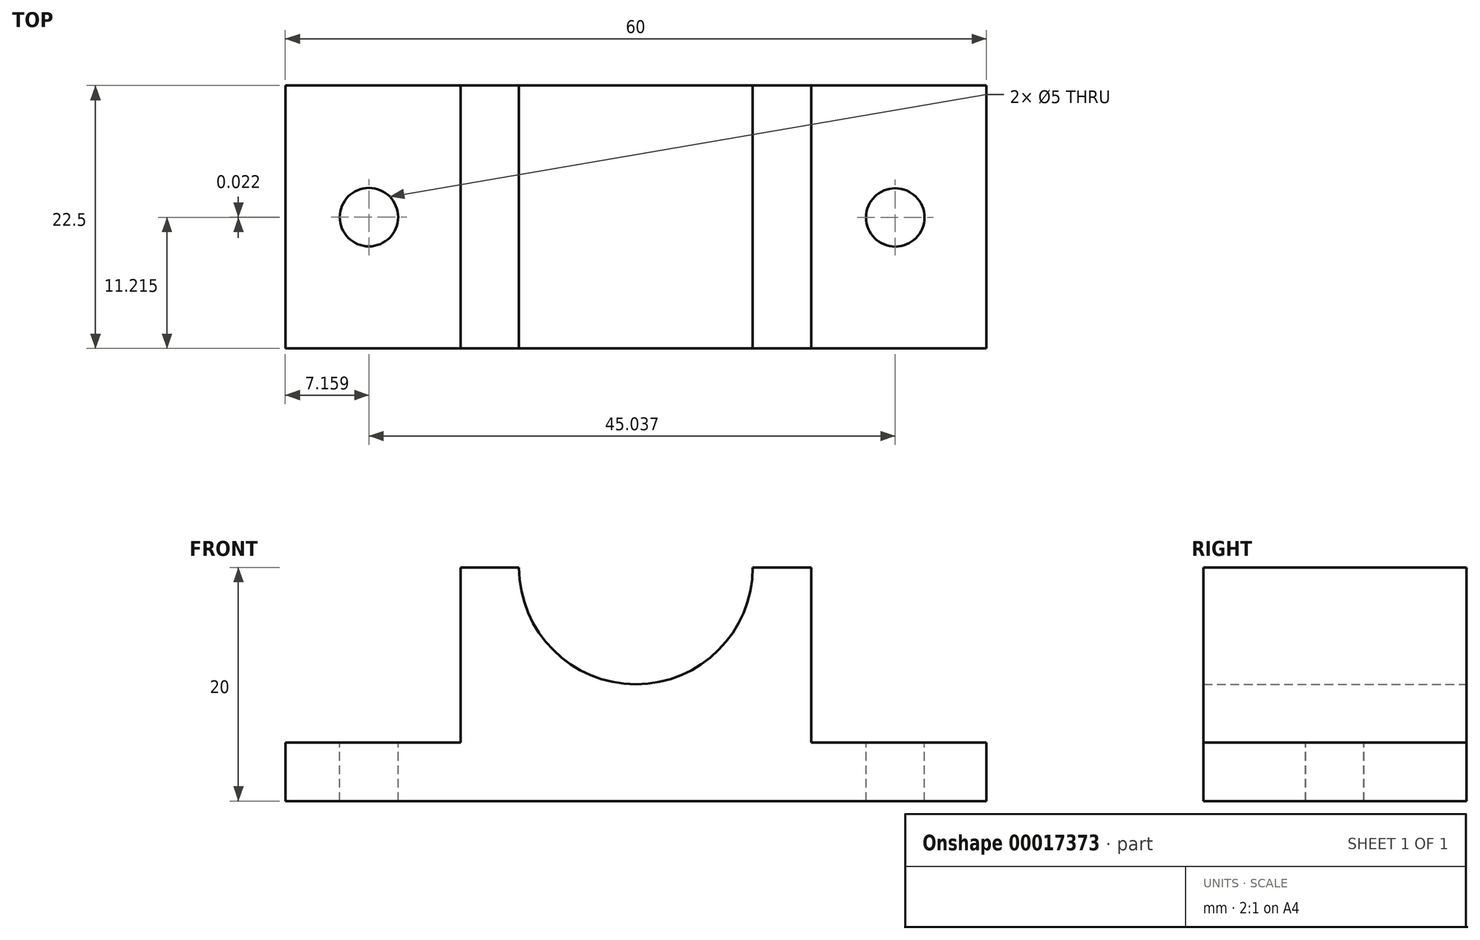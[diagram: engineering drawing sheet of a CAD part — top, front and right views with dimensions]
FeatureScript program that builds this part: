
annotation { "Feature Type Name" : "Feature", "Feature Type Description" : "" }
export const myFeature = defineFeature(function(context is Context, id is Id, definition is map)
    precondition{}
    {
        {
            var Q0;
            Q0=qCreatedBy(makeId("Front.planeOp"),FACE);
            var sketch = newSketch(context, id + "F0", { "sketchPlane" : qUnion([Q0])});
            skLineSegment(sketch, "E0", {"start": v(-35.29, 8.83) * mm, "end": v(24.71, 8.83) * mm});
            skLineSegment(sketch, "E1", {"start": v(24.71, 8.83) * mm, "end": v(24.71, 13.83) * mm});
            skLineSegment(sketch, "E2", {"start": v(24.71, 13.83) * mm, "end": v(9.71, 13.83) * mm});
            skLineSegment(sketch, "E3", {"start": v(9.71, 13.83) * mm, "end": v(9.71, 28.83) * mm});
            skLineSegment(sketch, "E4", {"start": v(9.71, 28.83) * mm, "end": v(4.71, 28.83) * mm});
            skLineSegment(sketch, "E5", {"start": v(-35.29, 13.83) * mm, "end": v(-35.29, 8.83) * mm});
            skLineSegment(sketch, "E6", {"start": v(-35.29, 13.83) * mm, "end": v(-20.29, 13.83) * mm});
            skLineSegment(sketch, "E7", {"start": v(-20.29, 13.83) * mm, "end": v(-20.29, 28.83) * mm});
            skLineSegment(sketch, "E8", {"start": v(-20.29, 28.83) * mm, "end": v(-15.29, 28.83) * mm});
            skArc(sketch, "E9", {"start": v(-15.29, 28.83) * mm, "mid": v(-5.29, 18.83) * mm, "end": v(4.71, 28.83) * mm});
            skSolve(sketch);
        }
        {
            var Q0;
            Q0=makeQuery(id+"F0.imprint","IMPRINT",FACE,{"disambiguationData":[TD([[makeQuery(id+"F0.imprint","IMPRINT",EDGE,{"derivedFrom":sQuery(id+"F0.wireOp",EDGE,"E0")}),1.0]])]});
            extrude(context, id + "F1", {"entities" : qUnion([Q0]), "depth" : 22.5 * mm});
        }
        {
            var Q0;
            Q0=makeQuery(id+"F1.opExtrude","SWEPT_FACE",FACE,{"disambiguationData":[OSD([sQuery(id+"F0.wireOp",EDGE,"E2")])]});
            var sketch = newSketch(context, id + "F2", { "sketchPlane" : qUnion([Q0])});
            skCircle(sketch, "E10", {"center": v(16.9, -11.28) * mm, "radius": 2.5 * mm});
            skSolve(sketch);
        }
        {
            var Q0;
            Q0=sQuery(id+"F2.wireOp",VERTEX,"E10.center");
            var Q1;
            Q1=makeQuery(id+"F1.opExtrude","SWEPT_BODY",BODY,{"disambiguationData":[OSD([sQuery(id+"F0.wireOp",EDGE,"E0"),sQuery(id+"F0.wireOp",EDGE,"E1"),sQuery(id+"F0.wireOp",EDGE,"E2"),sQuery(id+"F0.wireOp",EDGE,"E3"),sQuery(id+"F0.wireOp",EDGE,"E4"),sQuery(id+"F0.wireOp",EDGE,"E5"),sQuery(id+"F0.wireOp",EDGE,"E6"),sQuery(id+"F0.wireOp",EDGE,"E7"),sQuery(id+"F0.wireOp",EDGE,"E8"),sQuery(id+"F0.wireOp",EDGE,"d6d0405d-cb1b-481b-8e27-b3c6d3866435")])]});
            hole(context, id + "F3", {"style" : HoleStyle.SIMPLE, "holeDiameter" : 5 * mm, "endStyle" : HoleEndStyle.THROUGH, "locations" : qUnion([Q0]), "scope" : qUnion([Q1])});
        }
        {
            var Q0;
            Q0=makeQuery(id+"F1.opExtrude","SWEPT_FACE",FACE,{"disambiguationData":[OSD([sQuery(id+"F0.wireOp",EDGE,"E6")])]});
            var sketch = newSketch(context, id + "F4", { "sketchPlane" : qUnion([Q0])});
            skCircle(sketch, "E11", {"center": v(-28.13, -11.26) * mm, "radius": 2.5 * mm});
            skSolve(sketch);
        }
        {
            var Q0;
            Q0=sQuery(id+"F4.wireOp",VERTEX,"E11.center");
            var Q1;
            Q1=makeQuery(id+"F1.opExtrude","SWEPT_BODY",BODY,{"disambiguationData":[OSD([sQuery(id+"F0.wireOp",EDGE,"E0"),sQuery(id+"F0.wireOp",EDGE,"E1"),sQuery(id+"F0.wireOp",EDGE,"E2"),sQuery(id+"F0.wireOp",EDGE,"E3"),sQuery(id+"F0.wireOp",EDGE,"E4"),sQuery(id+"F0.wireOp",EDGE,"E5"),sQuery(id+"F0.wireOp",EDGE,"E6"),sQuery(id+"F0.wireOp",EDGE,"E7"),sQuery(id+"F0.wireOp",EDGE,"E8"),sQuery(id+"F0.wireOp",EDGE,"d6d0405d-cb1b-481b-8e27-b3c6d3866435")])]});
            hole(context, id + "F5", {"style" : HoleStyle.SIMPLE, "holeDiameter" : 5 * mm, "endStyle" : HoleEndStyle.THROUGH, "locations" : qUnion([Q0]), "scope" : qUnion([Q1])});
        }
    });
